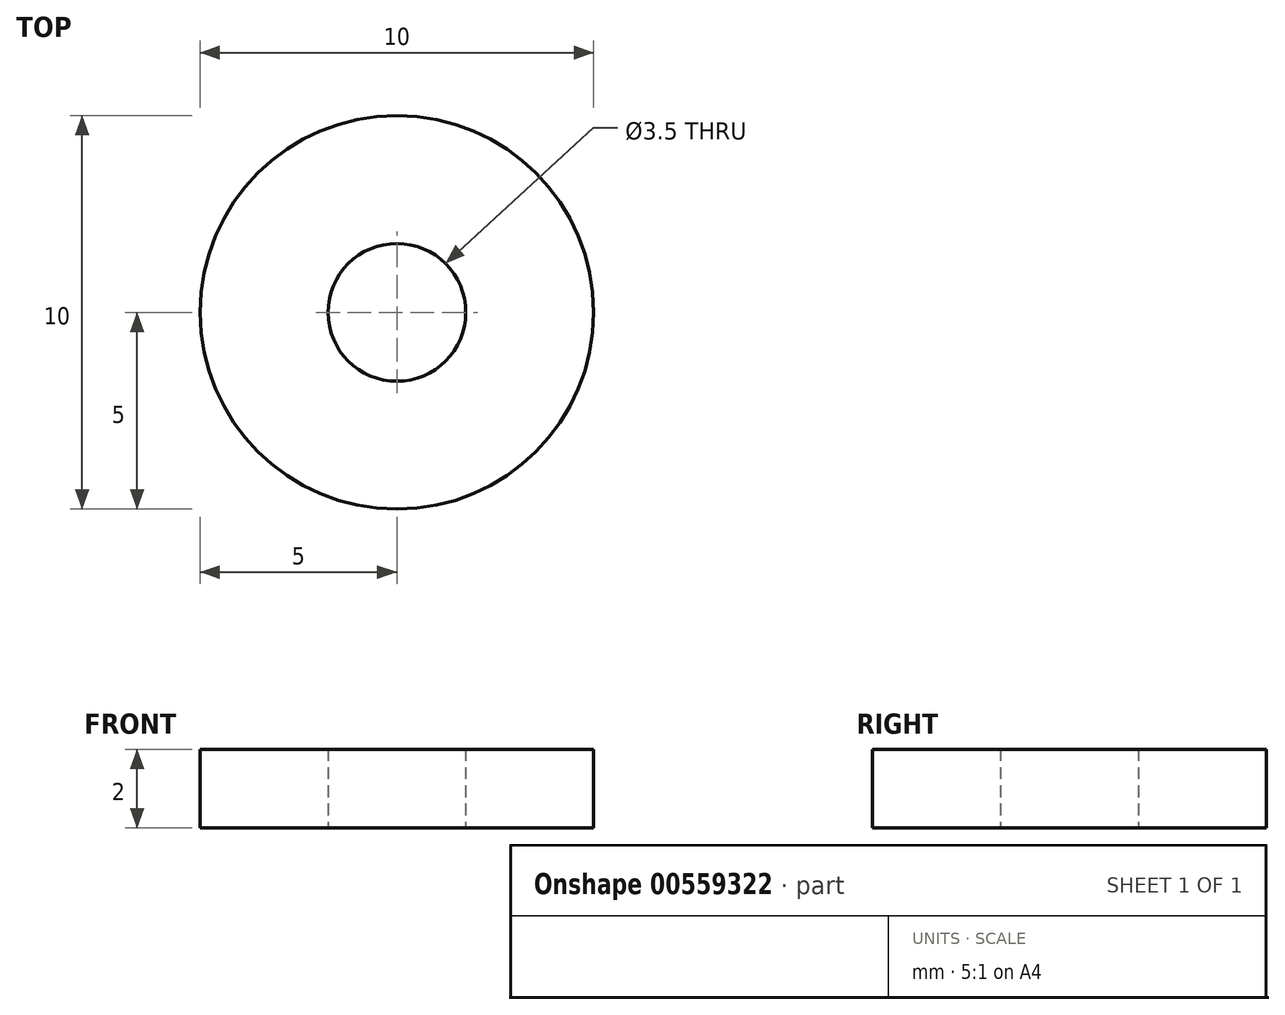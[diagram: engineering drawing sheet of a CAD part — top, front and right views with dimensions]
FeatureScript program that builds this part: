
annotation { "Feature Type Name" : "Feature", "Feature Type Description" : "" }
export const myFeature = defineFeature(function(context is Context, id is Id, definition is map)
    precondition{}
    {
        {
            var Q0;
            Q0=qCreatedBy(makeId("Top.planeOp"),FACE);
            var sketch = newSketch(context, id + "F0", { "sketchPlane" : qUnion([Q0])});
            skCircle(sketch, "E0", {"center": v(0, 0) * mm, "radius": 1.75 * mm});
            skCircle(sketch, "E1", {"center": v(0, 0) * mm, "radius": 5 * mm});
            skSolve(sketch);
        }
        {
            var Q0;
            Q0=makeQuery(id+"F0.imprint","IMPRINT",FACE,{"disambiguationData":[TD([[makeQuery(id+"F0.imprint","IMPRINT",EDGE,{"derivedFrom":sQuery(id+"F0.wireOp",EDGE,"E0")}),-1.0]])]});
            extrude(context, id + "F1", {"entities" : qUnion([Q0]), "depth" : 2 * mm, "offsetDistance" : 25 * mm});
        }
    });
